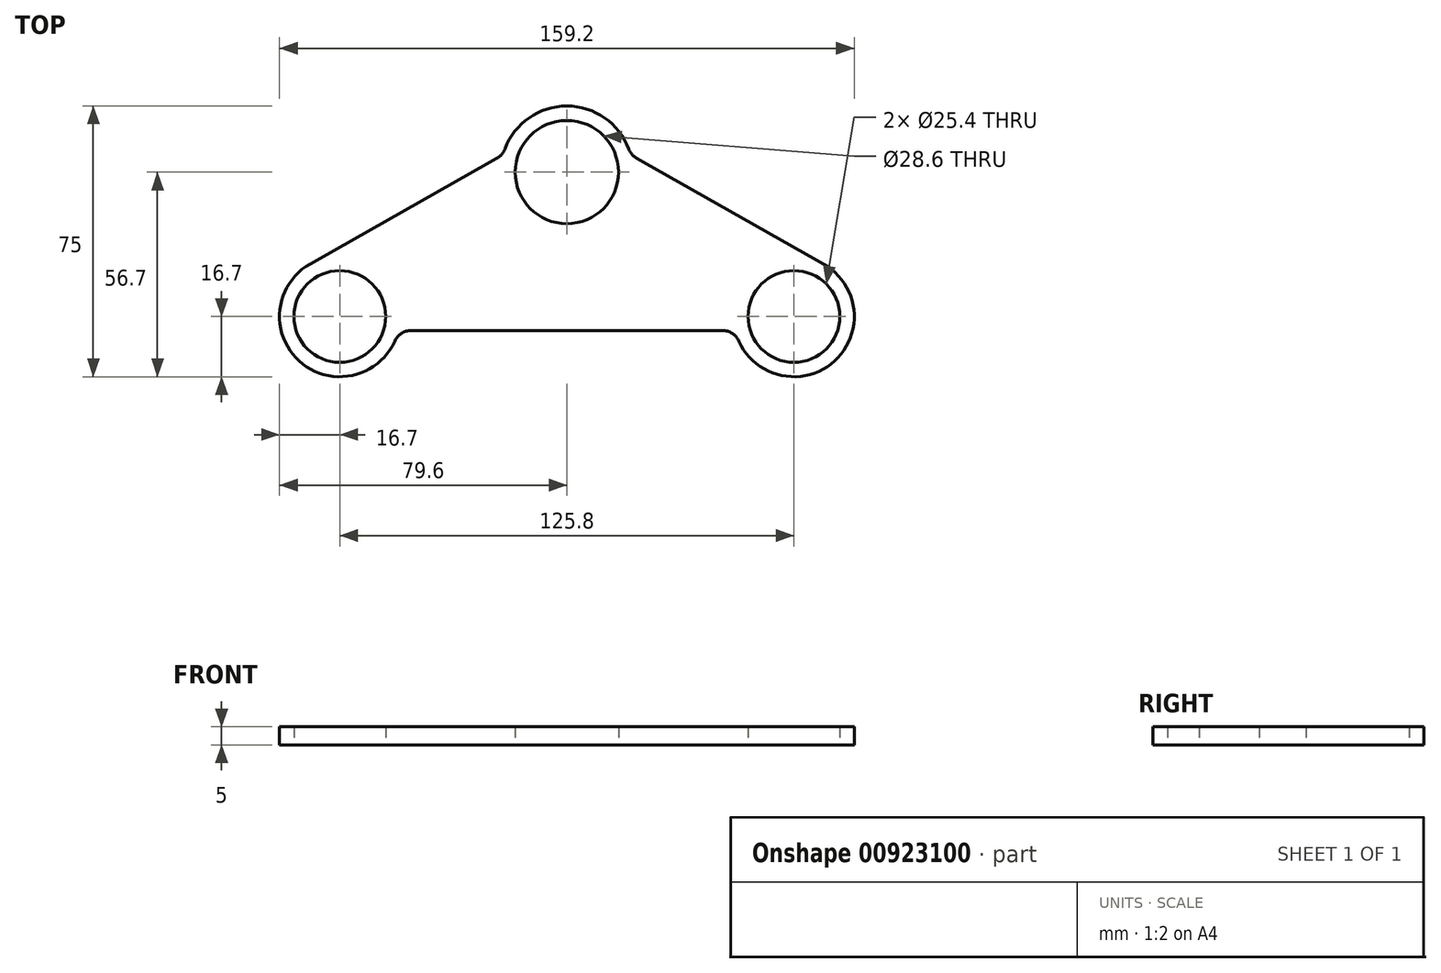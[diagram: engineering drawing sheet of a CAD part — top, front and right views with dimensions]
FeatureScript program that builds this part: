
annotation { "Feature Type Name" : "Feature", "Feature Type Description" : "" }
export const myFeature = defineFeature(function(context is Context, id is Id, definition is map)
    precondition{}
    {
        {
            var Q0;
            Q0=qCreatedBy(makeId("Top.planeOp"),FACE);
            var sketch = newSketch(context, id + "F0", { "sketchPlane" : qUnion([Q0])});
            skCircle(sketch, "E0", {"center": v(-62.9, -40) * mm, "radius": 12.7 * mm});
            skCircle(sketch, "E1", {"center": v(0, 0) * mm, "radius": 14.3 * mm});
            skCircle(sketch, "E2", {"center": v(62.9, -40) * mm, "radius": 12.7 * mm});
            skLineSegment(sketch, "E3", {"start": v(-62.9, -40) * mm, "end": v(62.9, -40) * mm, "construction": true});
            skPoint(sketch, "E4", {"position": v(-50.2, -40) * mm});
            skPoint(sketch, "E5", {"position": v(50.2, -40) * mm});
            skArc(sketch, "E6", {"start": v(-71.12, -25.47) * mm, "mid": v(-74.15, -52.34) * mm, "end": v(-47.67, -46.85) * mm});
            skLineSegment(sketch, "E7", {"start": v(-43.11, -43.9) * mm, "end": v(0, -43.9) * mm});
            skArc(sketch, "E8", {"start": v(0, 18.3) * mm, "mid": v(-10.42, 15.04) * mm, "end": v(-17.14, 6.42) * mm});
            skLineSegment(sketch, "E9", {"start": v(-19.36, 3.83) * mm, "end": v(-71.12, -25.47) * mm});
            skLineSegment(sketch, "E10", {"start": v(0, 18.3) * mm, "end": v(0, 14.3) * mm, "construction": true});
            skLineSegment(sketch, "E11", {"start": v(-75.6, -40) * mm, "end": v(-79.6, -40) * mm, "construction": true});
            skLineSegment(sketch, "E12", {"start": v(-50, -34.73) * mm, "end": v(-50, -45.85) * mm, "construction": true});
            skPoint(sketch, "E13.MirrorP", {"position": v(-49.8, -40) * mm});
            skLineSegment(sketch, "E14.MirrorCS", {"start": v(50, -34.73) * mm, "end": v(50, -45.85) * mm, "construction": true});
            skPoint(sketch, "E15.visualSharp", {"position": v(-46.66, -43.9) * mm});
            skArc(sketch, "E15.filletArc", {"start": v(-43.11, -43.9) * mm, "mid": v(-45.83, -44.7) * mm, "end": v(-47.67, -46.85) * mm});
            skPoint(sketch, "E16.visualSharp", {"position": v(-18.3, 0) * mm});
            skArc(sketch, "E16.filletArc", {"start": v(-19.36, 3.83) * mm, "mid": v(-18.02, 4.93) * mm, "end": v(-17.14, 6.42) * mm});
            skArc(sketch, "E17.MirrorCS", {"start": v(0, 18.3) * mm, "mid": v(10.42, 15.04) * mm, "end": v(17.14, 6.42) * mm});
            skArc(sketch, "E18.MirrorCS", {"start": v(19.36, 3.83) * mm, "mid": v(18.02, 4.93) * mm, "end": v(17.14, 6.42) * mm});
            skLineSegment(sketch, "E19.MirrorCS", {"start": v(19.36, 3.83) * mm, "end": v(71.12, -25.47) * mm});
            skArc(sketch, "E20.MirrorCS", {"start": v(71.12, -25.47) * mm, "mid": v(74.15, -52.34) * mm, "end": v(47.67, -46.85) * mm});
            skArc(sketch, "E21.MirrorCS", {"start": v(43.11, -43.9) * mm, "mid": v(45.83, -44.7) * mm, "end": v(47.67, -46.85) * mm});
            skLineSegment(sketch, "E22.MirrorCS", {"start": v(43.11, -43.9) * mm, "end": v(0, -43.9) * mm});
            skSolve(sketch);
        }
        {
            var Q0;
            Q0 = qSketchRegion(id + "F0", true);
            extrude(context, id + "F1", {"entities" : qUnion([Q0]), "endBound" : BoundingType.SYMMETRIC, "depth" : 5 * mm, "offsetDistance" : 25 * mm});
        }
    });
